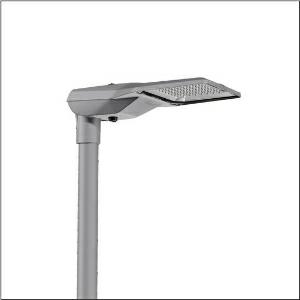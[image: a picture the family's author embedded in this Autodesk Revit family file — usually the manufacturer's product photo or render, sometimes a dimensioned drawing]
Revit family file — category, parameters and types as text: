
# Revit family: streetlight_sl_21_midi___st0_8a_5xe3c33t08mb_c889
name_source: partatom
category: Lighting Fixtures
units: mm (PartAtom-declared; Revit-internal decimal feet)

## family parameters
Cut with Voids When Loaded = No
Host = Face
Light Source = No
Part Type = Normal
Room Calculation Point = No
Round Connector Dimension = Use Diameter
Shared = No

## types (1)
- --- (1 x LED, 18270 lm, 136 W, 3000K)
    Apparent Load = 136 VA
    CIE Flux Codes = 38 75 97 100 100
    Color Rendering = 70
    Color Temperature = 3000K
    Default Elevation = 1800 mm
    Description = Streetlight SL 21 midi, mast luminaire, primary light control with lens, of PMMA, primary optical cover: cover, of toughened safety glass, transparent, light distribution: ST0.8a, light emission: direct distribution, primary light characteristic: asymmetric, installation type: side-entry, post-top, LED, High Power LED, rated luminous flux: 18.270lm, luminous efficacy: 134lm/W, light colour: 730, colour temperature: 3000K, control gear: D4i, control: overheat protection, constant luminous flux control, time-dependent luminous flux control, flexible luminous flux parameterisation, pre-setting: logarithmic dimming characteristic, mains connection: 230..240V, AC, 50/60Hz, start of lifetime: 136W, end of service life: 142W, reduction: 61W, luminaire housing, of diecast aluminium, powder-coated, Siteco® metallic grey (DB 702S), corrosivity category C5 mid according to DIN EN ISO 12944, please order mast flange separately, inclination adjustable: 0°, 5°, 10°, 15°, sealing non-destructively replaceable, multi-level sealing system, length: 644mm, width: 335mm, height: 110mm, mast flange for spigot size: 42mm (side-entry): 5XC10008XM4, 60/48mm (side-entry/post-top): 5XC10108XM2, 76/60mm (side-entry/post-top): 5XC10108XM1, mounting height: 4..8m, Smart Interface below and above, protection rating (complete): IP66, insulation class (complete): insulation class II (safety insulation), certification: CE, ENEC, ENEC+, VDE, impact resistance: IK10, permissible operating ambient temperature for outdoor applications: -40..+50°C, standard-compliant lighting for roads and squares, packaging unit: 1 piece

Light Distribution: ST0.8a
    Height = 111 mm
    Lamp = 1 x LED
    Lamp Light Flux = 18270 lm
    Lamp Power = 136 W
    Lamp count = 1
    Length = 644 mm
    Luminous efficacy = 134 lm/W
    Manufacturer = Siteco
    ModVariant = No
    Model = 5XE3C33T08MB
    Number of Poles = 1
    OnlyDefault = Yes
    Power Factor = 1
    Product Name = Streetlight SL 21 midi | ST0.8a
    Product group = mast luminaire | pylon top
    ProductGroupID = 6100
    Protection Class = Protection class II
    Protection Degree = IP 66
    RLX_Detail_Level = 1
    RLX_Emergency_Light_Flux = 0 lm
    RLX_Emergency_Type = 0
    RLX_Emergency_Type_DB = No
    RlxData = <blob elided: 27061 chars, md5=34ef2739>
    Socket = socket
    Standby Power = 0 W
    System Light Flux = 18270 lm
    System Power = 136 W
    Type Comments = factory setting: luminous flux: 100 % | dim-lin: 254 | 695 mA
    Type Image = l_1004304.jpg
    URL = http://relux.com
    VarID = @adj_186028
    Voltage = 0 V
    Weight = 0.00 kg
    Width = 336 mm

## geometry (parser evidence)
native form markers: Blend x4, Sweep x11
no freeform markers — native parametric forms only
